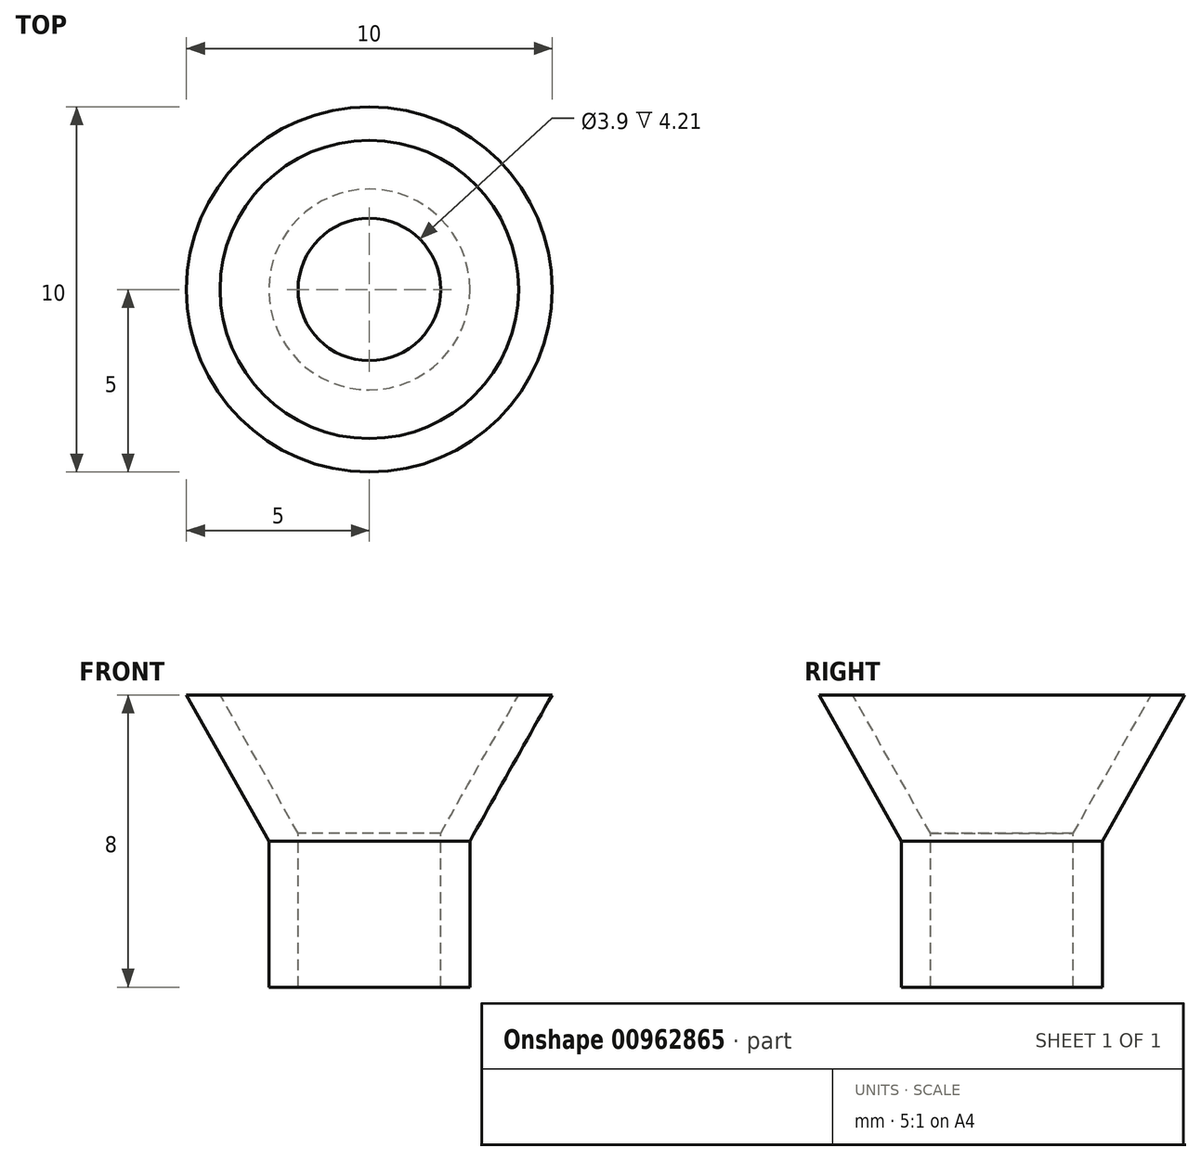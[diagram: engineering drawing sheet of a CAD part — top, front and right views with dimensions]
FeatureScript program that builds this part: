
annotation { "Feature Type Name" : "Feature", "Feature Type Description" : "" }
export const myFeature = defineFeature(function(context is Context, id is Id, definition is map)
    precondition{}
    {
        {
            var Q0;
            Q0=qCreatedBy(makeId("Top.planeOp"),FACE);
            var sketch = newSketch(context, id + "F0", { "sketchPlane" : qUnion([Q0])});
            skCircle(sketch, "E0", {"center": v(0, 0) * mm, "radius": 2.75 * mm});
            skSolve(sketch);
        }
        {
            var Q0;
            Q0=makeQuery(id+"F0.imprint","IMPRINT",FACE,{"disambiguationData":[TD([[makeQuery(id+"F0.imprint","IMPRINT",EDGE,{"derivedFrom":sQuery(id+"F0.wireOp",EDGE,"E0")}),1.0]])]});
            cPlane(context, id + "F1", {"entities" : qUnion([Q0]), "cplaneType" : CPlaneType.OFFSET, "offset" : 4 * mm, "width" : 150 * mm, "height" : 150 * mm});
        }
        {
            var Q0;
            Q0=qCreatedBy(id+"F1.planeOp",FACE);
            var sketch = newSketch(context, id + "F2", { "sketchPlane" : qUnion([Q0])});
            skPoint(sketch, "E1.0", {"position": v(0, 0) * mm});
            skCircle(sketch, "E2", {"center": v(0, 0) * mm, "radius": 5 * mm});
            skSolve(sketch);
        }
        {
            var Q0;
            Q0=makeQuery(id+"F0.imprint","IMPRINT",FACE,{"disambiguationData":[TD([[makeQuery(id+"F0.imprint","IMPRINT",EDGE,{"derivedFrom":sQuery(id+"F0.wireOp",EDGE,"E0")}),1.0]])]});
            cPlane(context, id + "F3", {"entities" : qUnion([Q0]), "cplaneType" : CPlaneType.OFFSET, "offset" : 4 * mm, "oppositeDirection" : true, "width" : 150 * mm, "height" : 150 * mm});
        }
        {
            var Q0;
            Q0=qCreatedBy(id+"F3.planeOp",FACE);
            var sketch = newSketch(context, id + "F4", { "sketchPlane" : qUnion([Q0])});
            skCircle(sketch, "E3.0", {"center": v(0, 0) * mm, "radius": 2.75 * mm});
            skSolve(sketch);
        }
        {
            var Q0;
            Q0=qCreatedBy(makeId("Front.planeOp"),FACE);
            var sketch = newSketch(context, id + "F5", { "sketchPlane" : qUnion([Q0])});
            skLineSegment(sketch, "E4.0", {"start": v(-2.75, -4) * mm, "end": v(2.75, -4) * mm});
            skLineSegment(sketch, "E5.0", {"start": v(-2.75, 0) * mm, "end": v(2.75, 0) * mm});
            skLineSegment(sketch, "E6", {"start": v(2.75, -4) * mm, "end": v(2.75, 0) * mm});
            skLineSegment(sketch, "E7", {"start": v(5, 4) * mm, "end": v(2.75, 0) * mm});
            skLineSegment(sketch, "E8.0", {"start": v(-5, 4) * mm, "end": v(5, 4) * mm});
            skSolve(sketch);
        }
        {
            var Q0;
            Q0=makeQuery(id+"F2.imprint","IMPRINT",FACE,{"disambiguationData":[TD([[makeQuery(id+"F2.imprint","IMPRINT",EDGE,{"derivedFrom":sQuery(id+"F2.wireOp",EDGE,"E2")}),1.0]])]});
            var Q1;
            Q1=makeQuery(id+"F0.imprint","IMPRINT",FACE,{"disambiguationData":[TD([[makeQuery(id+"F0.imprint","IMPRINT",EDGE,{"derivedFrom":sQuery(id+"F0.wireOp",EDGE,"E0")}),1.0]])]});
            var Q2;
            Q2=sQuery(id+"F5.wireOp",EDGE,"E7");
            loft(context, id + "F6", {"addGuides" : true, "sheetProfilesArray" : [{ "sheetProfileEntities" : qUnion([Q0]) }, { "sheetProfileEntities" : qUnion([Q1]) }], "guidesArray" : [{ "guideEntities" : qUnion([Q2]), "guideDerivativeType" : LoftGuideDerivativeType.DEFAULT, "guideDerivativeMagnitude" : 1 }]});
        }
        {
            var Q1;
            Q1=makeQuery(id+"F4.imprint","IMPRINT",FACE,{"disambiguationData":[TD([[makeQuery(id+"F4.imprint","IMPRINT",EDGE,{"derivedFrom":sQuery(id+"F4.wireOp",EDGE,"E3.0")}),1.0]])]});
            var Q2;
            Q2=makeQuery(id+"F6.opLoft","CAP_FACE",FACE,{"disambiguationData":[OSD([makeQuery(id+"F0.imprint","IMPRINT",FACE,{"disambiguationData":[TD([[makeQuery(id+"F0.imprint","IMPRINT",EDGE,{"derivedFrom":sQuery(id+"F0.wireOp",EDGE,"E0")}),1.0]])]})])],"isStart":true});
            loft(context, id + "F7", {"operationType" : NewBodyOperationType.ADD, "sheetProfilesArray" : [{ "sheetProfileEntities" : qUnion([Q1]) }, { "sheetProfileEntities" : qUnion([Q2]) }]});
        }
        {
            var Q0;
            Q0=makeQuery(id+"F6.opLoft","CAP_FACE",FACE,{"disambiguationData":[OSD([makeQuery(id+"F2.imprint","IMPRINT",FACE,{"disambiguationData":[TD([[makeQuery(id+"F2.imprint","IMPRINT",EDGE,{"derivedFrom":sQuery(id+"F2.wireOp",EDGE,"E2")}),1.0]])]})])],"isStart":true});
            var Q1;
            Q1=makeQuery(id+"F7.opLoft","CAP_FACE",FACE,{"disambiguationData":[OSD([makeQuery(id+"F4.imprint","IMPRINT",FACE,{"disambiguationData":[TD([[makeQuery(id+"F4.imprint","IMPRINT",EDGE,{"derivedFrom":sQuery(id+"F4.wireOp",EDGE,"E3.0")}),1.0]])]})])],"isStart":true});
            shell(context, id + "F8", {"entities" : qUnion([Q0, Q1]), "thickness" : .8 * mm});
        }
    });
